# Revit family: Aluco Skylight Therm (pl)
name_source: partatom
category: Modele ogólne
units: mm (PartAtom-declared; Revit-internal decimal feet)

## family parameters
Może być obiektem nadrzędnym dla zbrojenia = Nie
Numer OmniClass = 23.30.30.00
Oparty na płaszczyźnie roboczej = Tak
Punkt obliczania pomieszczeń = Nie
Tnij formami wycięć po wczytaniu = Nie
Typ części = Normalny
Tytuł OmniClass = Skylights
Współdzielony = Nie
Wymiar okrągłego złącza = Użyj średnicy
Zawsze pionowo = Nie

## types (1)
- Aluco Skylight Therm (pl)
    Domyślna rzędna = 0 mm  [stored 0 ft]
    IfcExportAs = "IfcWindowType"
    Klasa bezpieczeństwa pożarowego = BRoof (t1)
    Klasa bezpieczeństwa przed upadkiem z wysokości = SB 1200
    Komentarze do typu = Pasma świetlne łukowe
    Materiał podstawy = Aluco - stal ocynkowana
    Materiał profili = Aluco - aluminium
    Materiał płyt = Aluco - poliwęglan
    Model = Skylight Therm
    Obraz typu = ALUCO SKYLIGHT SL.png
    Odporność na obciążenie dociskające = DL 2500
    Odporność na obciążenie odrywające = UL 2500
    Opis = Pasma świetlne wykonane zgodnie z wymaganiami normy PN-EN14963:2006, ze znakowaniem CE
    Producent = ALUCO SYSTEM SP. Z O.O
    URL = https://aluco.com.pl
    URL produktu = https://aluco.com.pl

note: [stored X ft] marks values corroborated as IEEE doubles in the binary element streams (Revit-internal decimal feet)
